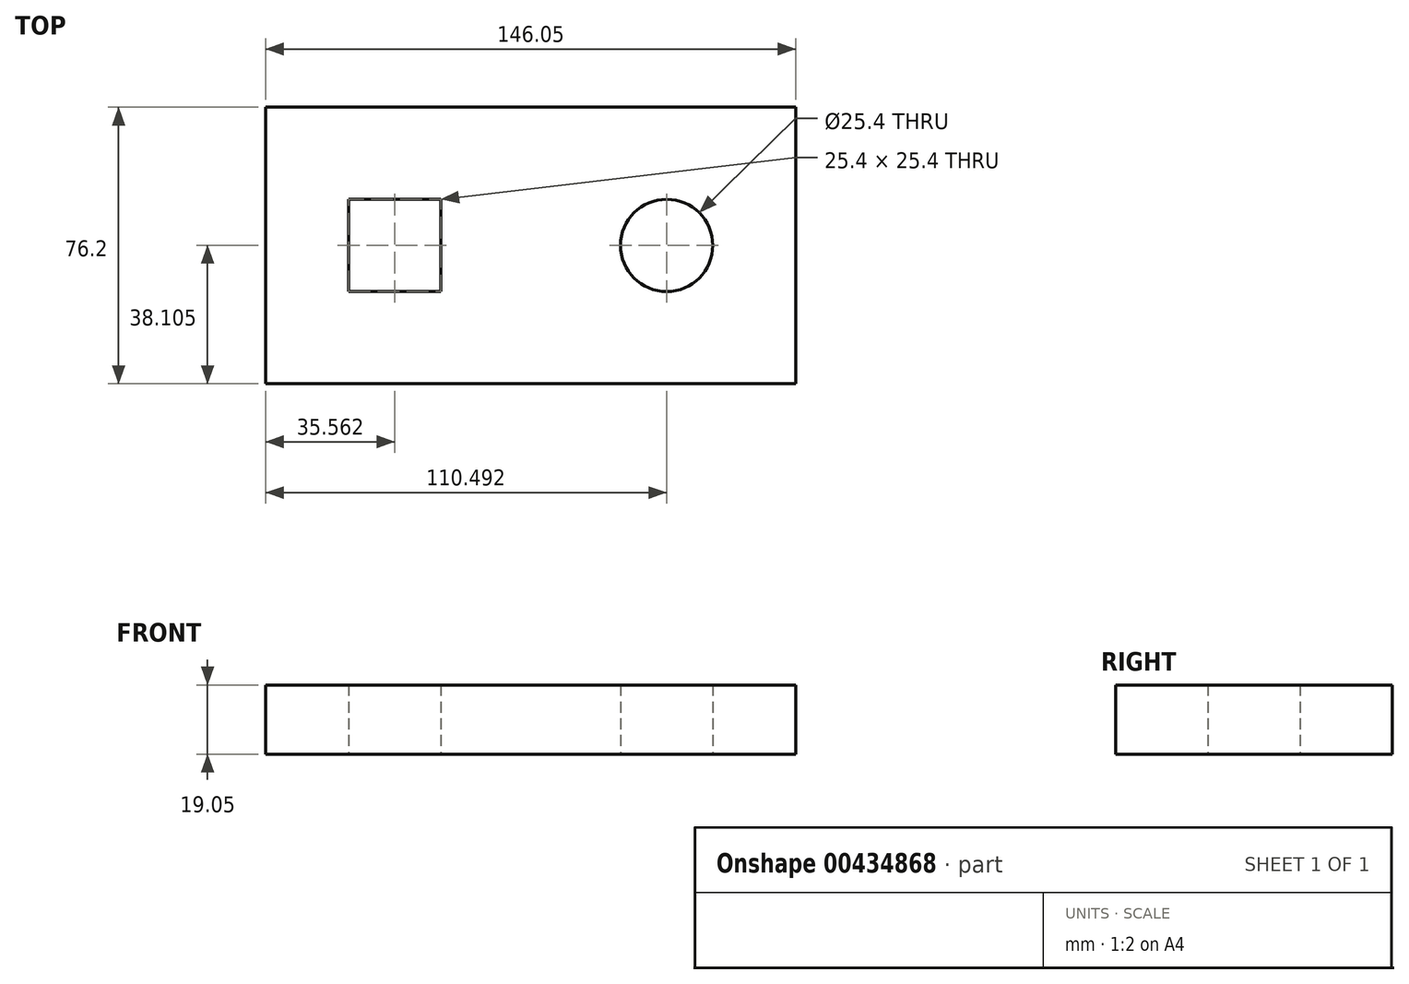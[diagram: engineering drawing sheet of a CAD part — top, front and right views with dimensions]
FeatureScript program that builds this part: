
annotation { "Feature Type Name" : "Feature", "Feature Type Description" : "" }
export const myFeature = defineFeature(function(context is Context, id is Id, definition is map)
    precondition{}
    {
        {
            var Q0;
            Q0=qCreatedBy(makeId("Top.planeOp"),FACE);
            var sketch = newSketch(context, id + "F0", { "sketchPlane" : qUnion([Q0])});
            skLineSegment(sketch, "E0.bottom", {"start": v(-73.68, 39.15) * mm, "end": v(72.37, 39.15) * mm});
            skLineSegment(sketch, "E0.top", {"start": v(-73.68, -37.05) * mm, "end": v(72.37, -37.05) * mm});
            skLineSegment(sketch, "E0.left", {"start": v(-73.68, 39.15) * mm, "end": v(-73.68, -37.05) * mm});
            skLineSegment(sketch, "E0.right", {"start": v(72.37, 39.15) * mm, "end": v(72.37, -37.05) * mm});
            skSolve(sketch);
        }
        {
            var Q0;
            Q0=makeQuery(id+"F0.imprint","IMPRINT",FACE,{"disambiguationData":[TD([[makeQuery(id+"F0.imprint","IMPRINT",EDGE,{"derivedFrom":sQuery(id+"F0.wireOp",EDGE,"E0.bottom")}),-1.0]])]});
            var sketch = newSketch(context, id + "F1", { "sketchPlane" : qUnion([Q0])});
            skLineSegment(sketch, "E1.bottom", {"start": v(-50.82, 13.75) * mm, "end": v(-25.42, 13.75) * mm});
            skLineSegment(sketch, "E1.top", {"start": v(-50.82, -11.65) * mm, "end": v(-25.42, -11.65) * mm});
            skLineSegment(sketch, "E1.left", {"start": v(-50.82, 13.75) * mm, "end": v(-50.82, -11.65) * mm});
            skLineSegment(sketch, "E1.right", {"start": v(-25.42, 13.75) * mm, "end": v(-25.42, -11.65) * mm});
            skSolve(sketch);
        }
        {
            var Q0;
            Q0=makeQuery(id+"F1.imprint","IMPRINT",FACE,{"disambiguationData":[TD([[makeQuery(id+"F1.imprint","IMPRINT",EDGE,{"derivedFrom":sQuery(id+"F1.wireOp",EDGE,"E1.bottom")}),1.0]])]});
            var sketch = newSketch(context, id + "F2", { "sketchPlane" : qUnion([Q0])});
            skCircle(sketch, "E2", {"center": v(36.81, 1.05) * mm, "radius": 12.7 * mm});
            skSolve(sketch);
        }
        {
            var Q0;
            Q0=makeQuery(id+"F1.imprint","IMPRINT",FACE,{"disambiguationData":[TD([[makeQuery(id+"F1.imprint","IMPRINT",EDGE,{"derivedFrom":sQuery(id+"F1.wireOp",EDGE,"E1.bottom")}),1.0]])]});
            extrude(context, id + "F3", {"entities" : qUnion([Q0]), "depth" : 19.05 * mm});
        }
        {
            var Q0;
            Q0 = qSketchRegion(id + "F2", true);
            extrude(context, id + "F4", {"entities" : qUnion([Q0]), "operationType" : NewBodyOperationType.REMOVE, "depth" : 36.83 * mm});
        }
    });
